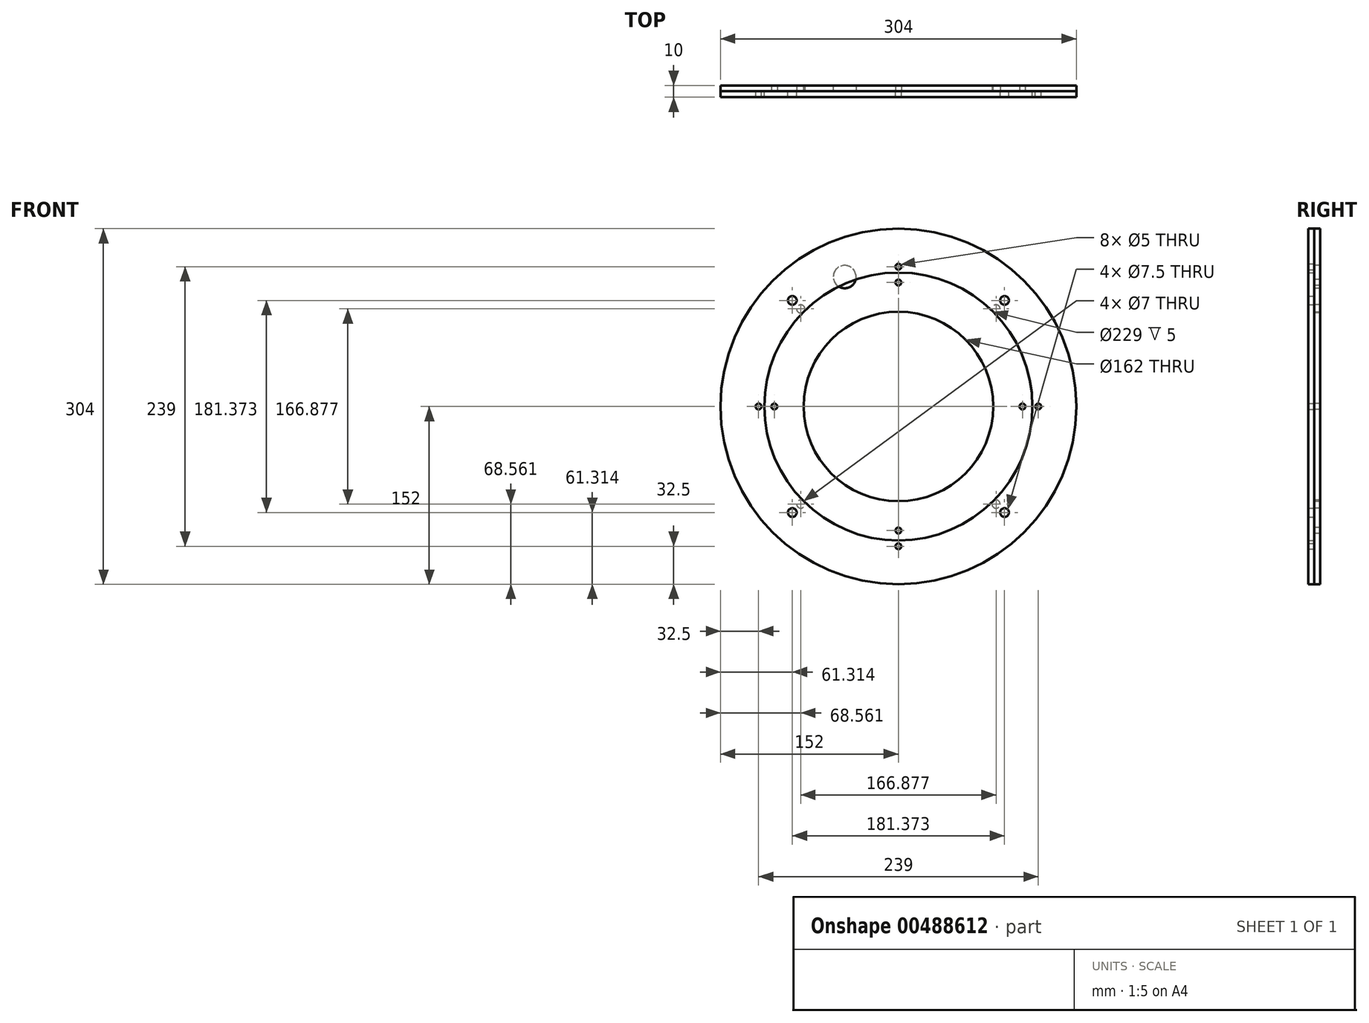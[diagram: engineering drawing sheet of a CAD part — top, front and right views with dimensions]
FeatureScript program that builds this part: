
annotation { "Feature Type Name" : "Feature", "Feature Type Description" : "" }
export const myFeature = defineFeature(function(context is Context, id is Id, definition is map)
    precondition{}
    {
        {
            var Q0;
            Q0=qCreatedBy(makeId("Front.planeOp"),FACE);
            var sketch = newSketch(context, id + "F0", { "sketchPlane" : qUnion([Q0])});
            skCircle(sketch, "E0", {"center": v(0, 0) * mm, "radius": 152 * mm});
            skCircle(sketch, "E1", {"center": v(0, 0) * mm, "radius": 81 * mm});
            skSolve(sketch);
        }
        {
            var Q0;
            Q0=makeQuery(id+"F0.imprint","IMPRINT",FACE,{"disambiguationData":[TD([[makeQuery(id+"F0.imprint","IMPRINT",EDGE,{"derivedFrom":sQuery(id+"F0.wireOp",EDGE,"E0")}),1.0]])]});
            extrude(context, id + "F1", {"entities" : qUnion([Q0]), "depth" : 5 * mm});
        }
        {
            var Q0;
            Q0=makeQuery(id+"F1.opExtrude","CAP_FACE",FACE,{"disambiguationData":[OSD([sQuery(id+"F0.wireOp",EDGE,"E0"),sQuery(id+"F0.wireOp",EDGE,"E1")])],"isStart":false});
            var sketch = newSketch(context, id + "F2", { "sketchPlane" : qUnion([Q0])});
            skCircle(sketch, "E2", {"center": v(0, 0) * mm, "radius": 106 * mm, "construction": true});
            skLineSegment(sketch, "E3", {"start": v(0, 0) * mm, "end": v(0, 106) * mm, "construction": true});
            skLineSegment(sketch, "E4", {"start": v(0, 0) * mm, "end": v(-106, 0) * mm, "construction": true});
            skLineSegment(sketch, "E5", {"start": v(0, 0) * mm, "end": v(0, -106) * mm, "construction": true});
            skLineSegment(sketch, "E6", {"start": v(0, 0) * mm, "end": v(106, 0) * mm, "construction": true});
            skCircle(sketch, "E7", {"center": v(0, 106) * mm, "radius": 2.5 * mm});
            skCircle(sketch, "E8", {"center": v(-106, 0) * mm, "radius": 2.5 * mm});
            skCircle(sketch, "E9", {"center": v(0, -106) * mm, "radius": 2.5 * mm});
            skCircle(sketch, "E10", {"center": v(106, 0) * mm, "radius": 2.5 * mm});
            skSolve(sketch);
        }
        {
            var Q0;
            Q0=makeQuery(id+"F2.imprint","IMPRINT",FACE,{"disambiguationData":[TD([[makeQuery(id+"F2.imprint","IMPRINT",EDGE,{"derivedFrom":sQuery(id+"F2.wireOp",EDGE,"E7")}),1.0]])]});
            extrude(context, id + "F3", {"entities" : qUnion([Q0]), "operationType" : NewBodyOperationType.REMOVE, "oppositeDirection" : true, "depth" : 5 * mm});
        }
        {
            var Q0;
            Q0=makeQuery(id+"F1.opExtrude","CAP_FACE",FACE,{"disambiguationData":[OSD([sQuery(id+"F0.wireOp",EDGE,"E0"),sQuery(id+"F0.wireOp",EDGE,"E1")])],"isStart":false});
            var sketch = newSketch(context, id + "F4", { "sketchPlane" : qUnion([Q0])});
            skSolve(sketch);
        }
        {
            var Q0;
            Q0=qSketchRegion(id+"F4",true);
            var Q1;
            Q1=makeQuery(id+"F2.imprint","IMPRINT",FACE,{"disambiguationData":[TD([[makeQuery(id+"F2.imprint","IMPRINT",EDGE,{"derivedFrom":sQuery(id+"F2.wireOp",EDGE,"E8")}),1.0]])]});
            extrude(context, id + "F5", {"entities" : qUnion([Q0, Q1]), "operationType" : NewBodyOperationType.REMOVE, "oppositeDirection" : true, "depth" : 5 * mm});
        }
        {
            var Q0;
            Q0=makeQuery(id+"F2.imprint","IMPRINT",FACE,{"disambiguationData":[TD([[makeQuery(id+"F2.imprint","IMPRINT",EDGE,{"derivedFrom":sQuery(id+"F2.wireOp",EDGE,"E9")}),1.0]])]});
            extrude(context, id + "F6", {"entities" : qUnion([Q0]), "operationType" : NewBodyOperationType.REMOVE, "oppositeDirection" : true, "depth" : 5 * mm});
        }
        {
            var Q0;
            Q0=makeQuery(id+"F2.imprint","IMPRINT",FACE,{"disambiguationData":[TD([[makeQuery(id+"F2.imprint","IMPRINT",EDGE,{"derivedFrom":sQuery(id+"F2.wireOp",EDGE,"E10")}),1.0]])]});
            extrude(context, id + "F7", {"entities" : qUnion([Q0]), "operationType" : NewBodyOperationType.REMOVE, "oppositeDirection" : true, "depth" : 5 * mm});
        }
        {
            var Q0;
            Q0=makeQuery(id+"F4.imprint","IMPRINT",FACE,{"disambiguationData":[TD([[makeQuery(id+"F4.imprint","IMPRINT",EDGE,{"derivedFrom":makeQuery(id+"F1.opExtrude","CAP_EDGE",EDGE,{"disambiguationData":[OSD([sQuery(id+"F0.wireOp",EDGE,"E0")])],"isStart":false})}),1.0]])]});
            var sketch = newSketch(context, id + "F8", { "sketchPlane" : qUnion([Q0])});
            skLineSegment(sketch, "E11", {"start": v(0, 0) * mm, "end": v(83.44, 83.44) * mm, "construction": true});
            skCircle(sketch, "E12", {"center": v(0, 0) * mm, "radius": 118 * mm, "construction": true});
            skLineSegment(sketch, "E13", {"start": v(0, 0) * mm, "end": v(83.44, -83.44) * mm, "construction": true});
            skLineSegment(sketch, "E14", {"start": v(0, 0) * mm, "end": v(-83.44, 83.44) * mm, "construction": true});
            skLineSegment(sketch, "E15", {"start": v(0, 0) * mm, "end": v(-83.44, -83.44) * mm, "construction": true});
            skCircle(sketch, "E16", {"center": v(83.44, 83.44) * mm, "radius": 3.5 * mm});
            skCircle(sketch, "E17", {"center": v(83.44, -83.44) * mm, "radius": 3.5 * mm});
            skCircle(sketch, "E18", {"center": v(-83.44, -83.44) * mm, "radius": 3.5 * mm});
            skCircle(sketch, "E19", {"center": v(-83.44, 83.44) * mm, "radius": 3.5 * mm});
            skLineSegment(sketch, "E20", {"start": v(0, 0) * mm, "end": v(-45.92, 110.87) * mm, "construction": true});
            skCircle(sketch, "E21", {"center": v(-45.92, 110.87) * mm, "radius": 9.75 * mm});
            skSolve(sketch);
        }
        {
            var Q0;
            Q0=qSketchRegion(id+"F8",true);
            var Q1;
            Q1=makeQuery(id+"F1.opExtrude","CAP_FACE",FACE,{"disambiguationData":[OSD([sQuery(id+"F0.wireOp",EDGE,"E0"),sQuery(id+"F0.wireOp",EDGE,"E1")])],"isStart":true});
            extrude(context, id + "F9", {"entities" : qUnion([Q0]), "operationType" : NewBodyOperationType.REMOVE, "endBound" : BoundingType.UP_TO_SURFACE, "oppositeDirection" : true, "endBoundEntityFace" : qUnion([Q1]), "depth" : 5 * mm});
        }
        {
            var Q0;
            Q0=makeQuery(id+"F2.imprint","IMPRINT",FACE,{"disambiguationData":[TD([[makeQuery(id+"F2.imprint","IMPRINT",EDGE,{"derivedFrom":sQuery(id+"F2.wireOp",EDGE,"E7")}),-1.0]])]});
            var sketch = newSketch(context, id + "F10", { "sketchPlane" : qUnion([Q0])});
            skCircle(sketch, "E22", {"center": v(0, 0) * mm, "radius": 152 * mm});
            skCircle(sketch, "E23", {"center": v(0, 0) * mm, "radius": 114.5 * mm});
            skCircle(sketch, "E24", {"center": v(0, 0) * mm, "radius": 119.5 * mm, "construction": true});
            skLineSegment(sketch, "E25", {"start": v(0, 0) * mm, "end": v(0, 119.5) * mm, "construction": true});
            skLineSegment(sketch, "E26", {"start": v(0, 0) * mm, "end": v(0, -119.5) * mm, "construction": true});
            skLineSegment(sketch, "E27", {"start": v(0, 0) * mm, "end": v(-119.5, 0) * mm, "construction": true});
            skLineSegment(sketch, "E28", {"start": v(0, 0) * mm, "end": v(119.5, 0) * mm, "construction": true});
            skCircle(sketch, "E29", {"center": v(0, 119.5) * mm, "radius": 2.5 * mm});
            skCircle(sketch, "E30", {"center": v(-119.5, 0) * mm, "radius": 2.5 * mm});
            skCircle(sketch, "E31", {"center": v(0, -119.5) * mm, "radius": 2.5 * mm});
            skCircle(sketch, "E32", {"center": v(119.5, 0) * mm, "radius": 2.5 * mm});
            skCircle(sketch, "E33", {"center": v(0, 0) * mm, "radius": 128.25 * mm, "construction": true});
            skLineSegment(sketch, "E34", {"start": v(0, 0) * mm, "end": v(-90.69, 90.69) * mm, "construction": true});
            skLineSegment(sketch, "E35", {"start": v(0, 0) * mm, "end": v(-90.69, -90.69) * mm, "construction": true});
            skLineSegment(sketch, "E36", {"start": v(0, 0) * mm, "end": v(90.69, 90.69) * mm, "construction": true});
            skLineSegment(sketch, "E37", {"start": v(0, 0) * mm, "end": v(90.69, -90.69) * mm, "construction": true});
            skCircle(sketch, "E38", {"center": v(-90.69, 90.69) * mm, "radius": 3.75 * mm});
            skCircle(sketch, "E39", {"center": v(-90.69, -90.69) * mm, "radius": 3.75 * mm});
            skCircle(sketch, "E40", {"center": v(90.69, -90.69) * mm, "radius": 3.75 * mm});
            skCircle(sketch, "E41", {"center": v(90.69, 90.69) * mm, "radius": 3.75 * mm});
            skSolve(sketch);
        }
        {
            var Q0;
            Q0=qSketchRegion(id+"F10",true);
            extrude(context, id + "F11", {"entities" : qUnion([Q0]), "depth" : 5 * mm});
        }
    });
